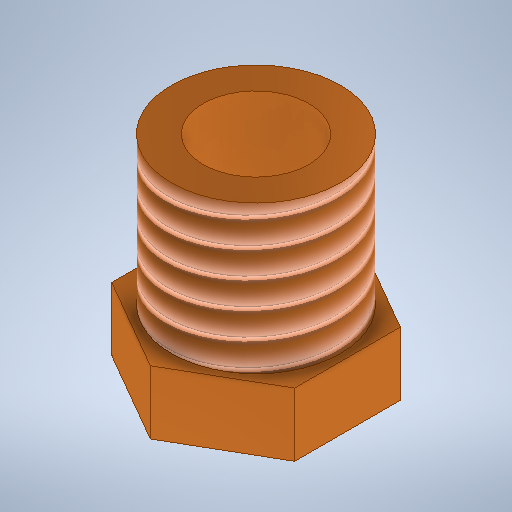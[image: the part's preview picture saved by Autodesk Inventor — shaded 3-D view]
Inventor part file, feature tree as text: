
AUTODESK INVENTOR PART (.ipt)
format: ipt  version: 2025.1 (Build 291241000, 241)  size: 338,432 bytes
history: native  units: mm
features: sketch x3, extrude x2, hole x1, thread x1
ambient origin geometry x8: Origin, YZ Plane, XZ Plane, XY Plane, X Axis, Y Axis, Z Axis, Center Point
bodies: Solid1 (feature_tree)
feature tree (7):
  extrude  "Extrusion1"  Depth=3.0mm TaperAngle=0.0deg
  extrude  "Extrusion2"  Depth=7.0mm TaperAngle=0.0deg
  hole  "Hole1"  [1 undecoded]
  thread  "Thread1"  [1 undecoded]
  sketch  "Sketch1"  dims[d0=10.0mm d1=3.0mm d2=0.0mm]
  sketch  "Sketch2"  dims[d3=8.0mm d4=7.0mm d5=0.0mm]
  sketch  "Sketch3"  dims[d6=5.0mm d7=6.0mm d8=4.0mm d9=2.0mm d10=90.0deg d11=6.0mm d12=0.0mm d13=7.0mm d14=0.0mm]
note: 2 required parameter values undecoded (feature->parameter linkage not recoverable at this tier; creation-order binding heuristic only, values carry confidence <= 0.55)
